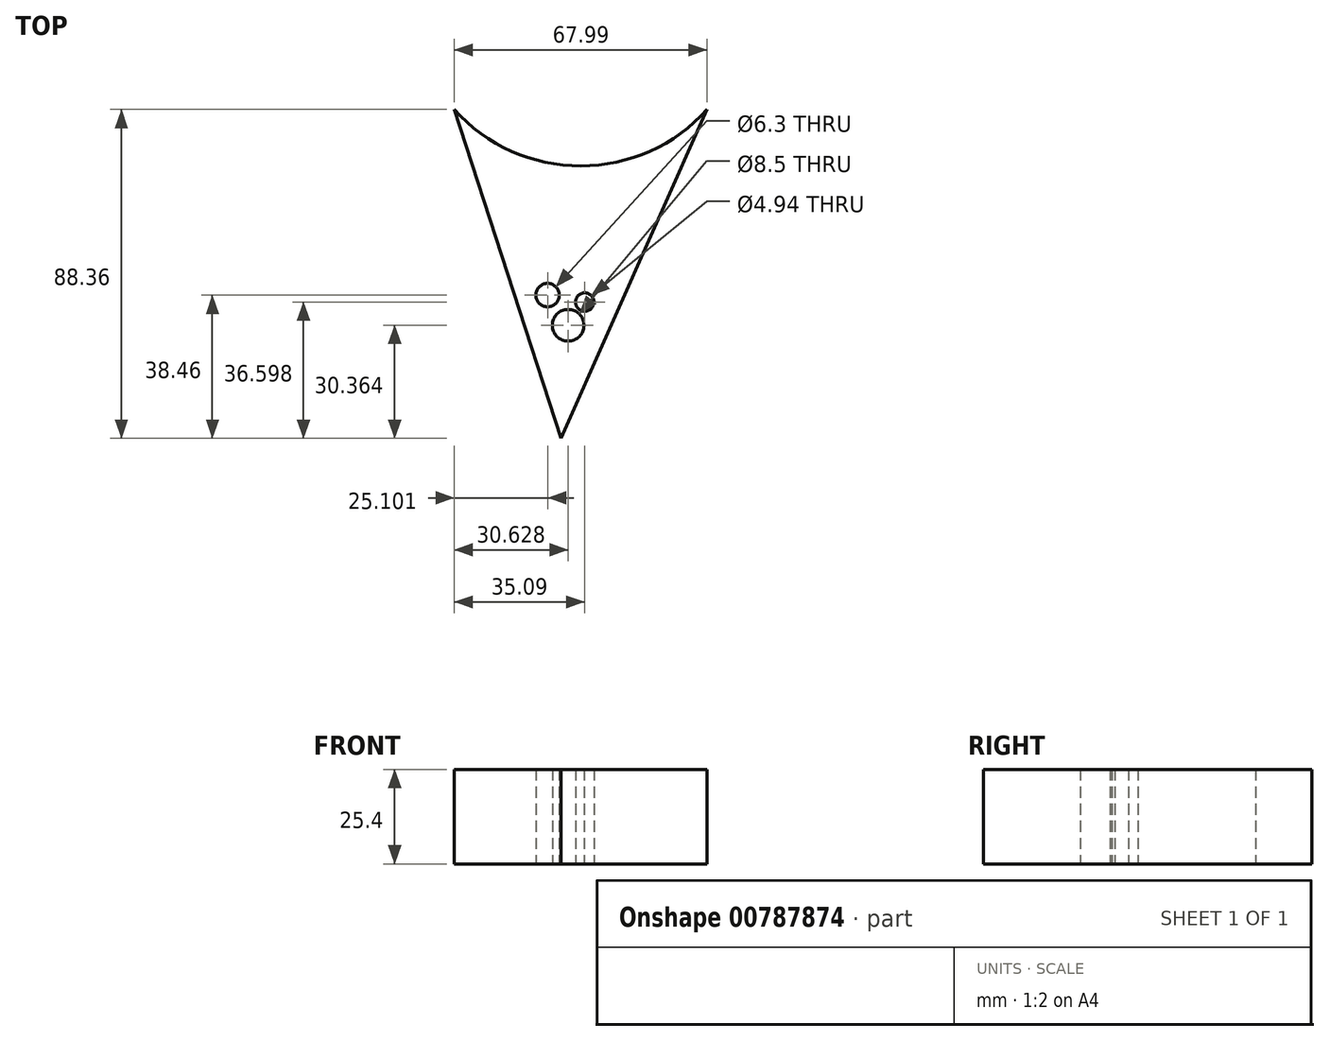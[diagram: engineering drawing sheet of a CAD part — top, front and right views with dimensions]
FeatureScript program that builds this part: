
annotation { "Feature Type Name" : "Feature", "Feature Type Description" : "" }
export const myFeature = defineFeature(function(context is Context, id is Id, definition is map)
    precondition{}
    {
        {
            var Q0;
            Q0=qCreatedBy(makeId("Top.planeOp"),FACE);
            var sketch = newSketch(context, id + "F0", { "sketchPlane" : qUnion([Q0])});
            skArc(sketch, "E0", {"start": v(-42.56, 34.15) * mm, "mid": v(-8.56, 18.96) * mm, "end": v(25.43, 34.15) * mm});
            skLineSegment(sketch, "E1", {"start": v(-42.56, 34.15) * mm, "end": v(-13.87, -54.21) * mm});
            skLineSegment(sketch, "E2", {"start": v(-13.87, -54.21) * mm, "end": v(25.43, 34.15) * mm});
            skCircle(sketch, "E3", {"center": v(-11.93, -23.85) * mm, "radius": 4.25 * mm});
            skCircle(sketch, "E4", {"center": v(-17.46, -15.75) * mm, "radius": 3.15 * mm});
            skCircle(sketch, "E5", {"center": v(-7.47, -17.61) * mm, "radius": 2.47 * mm});
            skSolve(sketch);
        }
        {
            var Q0;
            Q0=makeQuery(id+"F0.imprint","IMPRINT",FACE,{"disambiguationData":[TD([[makeQuery(id+"F0.imprint","IMPRINT",EDGE,{"derivedFrom":sQuery(id+"F0.wireOp",EDGE,"E0")}),-1.0]])]});
            extrude(context, id + "F1", {"entities" : qUnion([Q0]), "depth" : 25.4 * mm, "offsetDistance" : 25.4 * mm});
        }
    });
